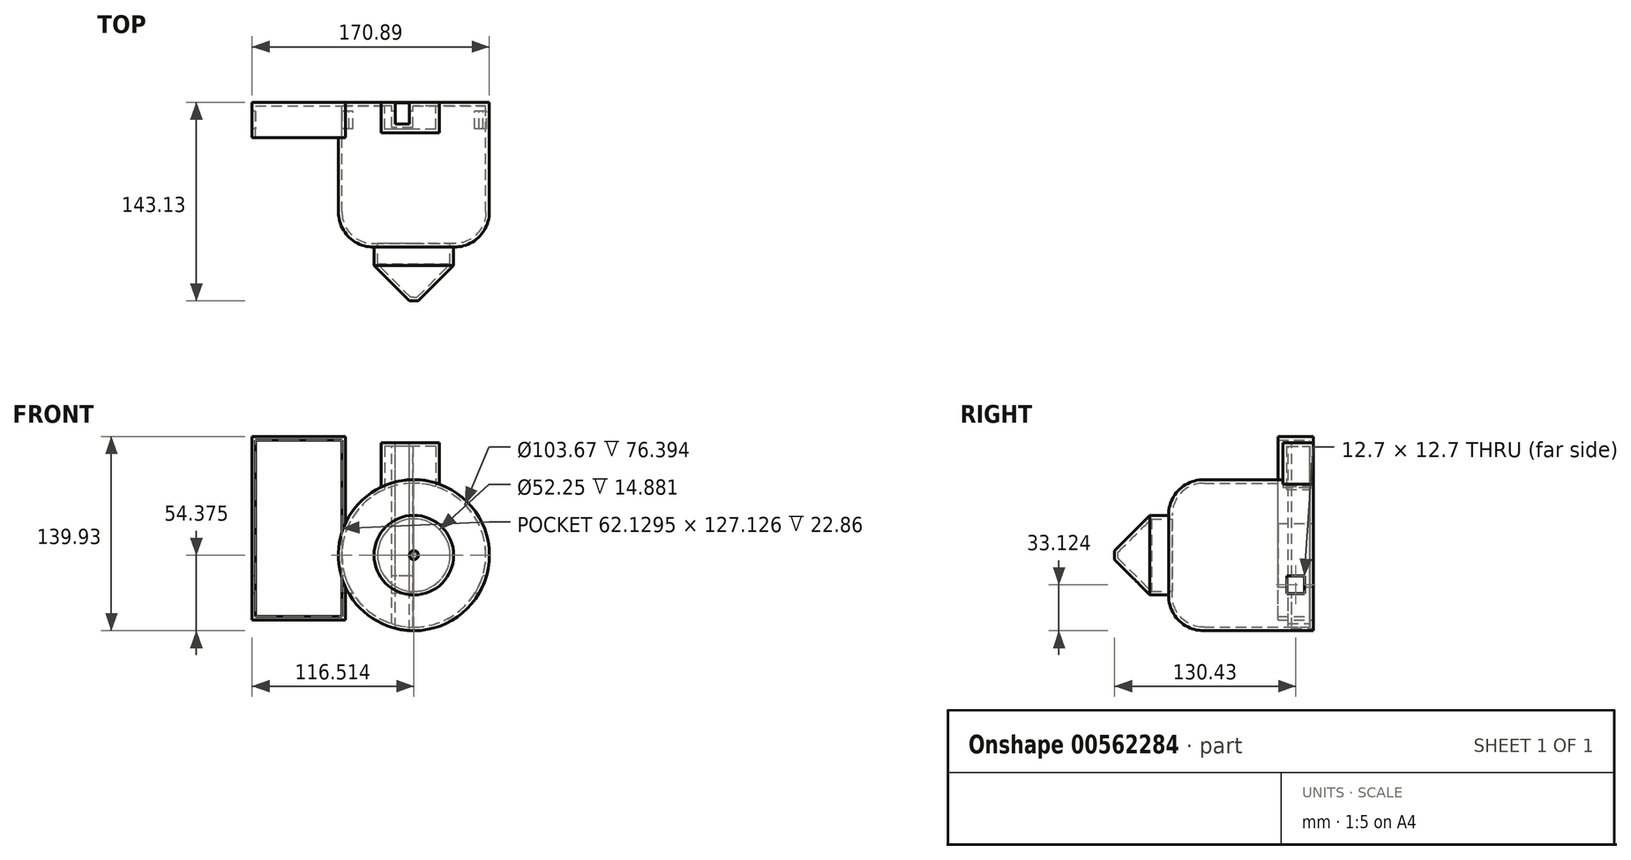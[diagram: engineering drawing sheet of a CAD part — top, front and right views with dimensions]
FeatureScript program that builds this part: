
annotation { "Feature Type Name" : "Feature", "Feature Type Description" : "" }
export const myFeature = defineFeature(function(context is Context, id is Id, definition is map)
    precondition{}
    {
        {
            var Q0;
            Q0=qCreatedBy(makeId("Front.planeOp"),FACE);
            var sketch = newSketch(context, id + "F0", { "sketchPlane" : qUnion([Q0])});
            skCircle(sketch, "E0", {"center": v(49.3, -22.93) * mm, "radius": 54.37 * mm});
            skSolve(sketch);
        }
        {
            var Q0;
            Q0 = qSketchRegion(id + "F0", true);
            extrude(context, id + "F1", {"entities" : qUnion([Q0]), "depth" : 104.33 * mm, "offsetDistance" : 25.4 * mm});
        }
        {
            var Q0;
            Q0=qCreatedBy(makeId("Front.planeOp"),FACE);
            var sketch = newSketch(context, id + "F2", { "sketchPlane" : qUnion([Q0])});
            skLineSegment(sketch, "E1.bottom", {"start": v(67.62, 57.92) * mm, "end": v(25.77, 57.92) * mm});
            skLineSegment(sketch, "E1.top", {"start": v(67.62, 15.74) * mm, "end": v(25.77, 15.74) * mm});
            skLineSegment(sketch, "E1.left", {"start": v(67.62, 57.92) * mm, "end": v(67.62, 15.74) * mm});
            skLineSegment(sketch, "E1.right", {"start": v(25.77, 57.92) * mm, "end": v(25.77, 15.74) * mm});
            skLineSegment(sketch, "E2.bottom", {"start": v(-64.32, 213.68) * mm, "end": v(12.28, 213.68) * mm});
            skLineSegment(sketch, "E2.top", {"start": v(-64.32, 129.94) * mm, "end": v(12.28, 129.94) * mm});
            skLineSegment(sketch, "E2.left", {"start": v(-64.32, 213.68) * mm, "end": v(-64.32, 129.94) * mm});
            skLineSegment(sketch, "E2.right", {"start": v(12.28, 213.68) * mm, "end": v(12.28, 129.94) * mm});
            skSolve(sketch);
        }
        {
            var Q0;
            Q0=makeQuery(id+"F2.imprint","IMPRINT",FACE,{"disambiguationData":[TD([[makeQuery(id+"F2.imprint","IMPRINT",EDGE,{"derivedFrom":sQuery(id+"F2.wireOp",EDGE,"E1.bottom")}),1.0]])]});
            extrude(context, id + "F3", {"entities" : qUnion([Q0]), "operationType" : NewBodyOperationType.ADD, "depth" : 22.02 * mm, "offsetDistance" : 25.4 * mm});
        }
        {
            var Q0;
            Q0=makeQuery(id+"F1.opExtrude","CAP_EDGE",EDGE,{"disambiguationData":[OSD([sQuery(id+"F0.wireOp",EDGE,"E0")])],"isStart":false});
            fillet(context, id + "F4", {"entities" : qUnion([Q0]), "radius" : 25.4 * mm, "tangentPropagation" : true, "allowEdgeOverflow" : false});
        }
        {
            var Q0;
            Q0=makeQuery(id+"F1.opExtrude","CAP_FACE",FACE,{"disambiguationData":[OSD([sQuery(id+"F0.wireOp",EDGE,"E0")])],"isStart":false});
            var sketch = newSketch(context, id + "F5", { "sketchPlane" : qUnion([Q0])});
            skCircle(sketch, "E3", {"center": v(49.3, -22.93) * mm, "radius": 28.66 * mm});
            skSolve(sketch);
        }
        {
            var Q0;
            Q0 = qSketchRegion(id + "F5", true);
            extrude(context, id + "F6", {"entities" : qUnion([Q0]), "operationType" : NewBodyOperationType.ADD, "depth" : 38.8 * mm, "offsetDistance" : 25.4 * mm});
        }
        {
            var Q0;
            Q0=makeQuery(id+"F6.opExtrude","CAP_EDGE",EDGE,{"disambiguationData":[OSD([sQuery(id+"F5.wireOp",EDGE,"E3")])],"isStart":false});
            chamfer(context, id + "F7", {"entities" : qUnion([Q0]), "width" : 25.4 * mm, "tangentPropagation" : true});
        }
        {
            var Q0;
            Q0=makeQuery(id+"F3.opExtrude","SWEPT_FACE",FACE,{"disambiguationData":[OSD([sQuery(id+"F2.wireOp",EDGE,"E1.bottom")])]});
            var sketch = newSketch(context, id + "F8", { "sketchPlane" : qUnion([Q0])});
            skLineSegment(sketch, "E4.bottom", {"start": v(46.1, -15.67) * mm, "end": v(35.93, -15.67) * mm});
            skLineSegment(sketch, "E4.top", {"start": v(46.1, -0.43) * mm, "end": v(35.93, -0.43) * mm});
            skLineSegment(sketch, "E4.left", {"start": v(46.1, -15.67) * mm, "end": v(46.1, -0.43) * mm});
            skLineSegment(sketch, "E4.right", {"start": v(35.93, -15.67) * mm, "end": v(35.93, -0.43) * mm});
            skSolve(sketch);
        }
        {
            var Q0;
            Q0=makeQuery(id+"F8.imprint","IMPRINT",FACE,{"disambiguationData":[TD([[makeQuery(id+"F8.imprint","IMPRINT",EDGE,{"derivedFrom":sQuery(id+"F8.wireOp",EDGE,"E4.bottom")}),-1.0]])]});
            extrude(context, id + "F9", {"entities" : qUnion([Q0]), "operationType" : NewBodyOperationType.REMOVE, "endBound" : BoundingType.THROUGH_ALL, "oppositeDirection" : true, "depth" : 25.4 * mm, "offsetDistance" : 25.4 * mm});
        }
        {
            var Q0;
            Q0=qCreatedBy(makeId("Front.planeOp"),FACE);
            var sketch = newSketch(context, id + "F10", { "sketchPlane" : qUnion([Q0])});
            skLineSegment(sketch, "E5.bottom", {"start": v(-67.2, -69.58) * mm, "end": v(0, -69.58) * mm});
            skLineSegment(sketch, "E5.top", {"start": v(-67.2, 62.63) * mm, "end": v(0, 62.63) * mm});
            skLineSegment(sketch, "E5.left", {"start": v(-67.2, -69.58) * mm, "end": v(-67.2, 62.63) * mm});
            skLineSegment(sketch, "E5.right", {"start": v(0, -69.58) * mm, "end": v(0, 62.63) * mm});
            skSolve(sketch);
        }
        {
            var Q0;
            Q0 = qSketchRegion(id + "F10", true);
            extrude(context, id + "F11", {"entities" : qUnion([Q0]), "operationType" : NewBodyOperationType.ADD, "depth" : 25.4 * mm, "offsetDistance" : 25.4 * mm});
        }
        {
            var Q0;
            Q0=makeQuery(id+"F11.opExtrude","CAP_FACE",FACE,{"disambiguationData":[OSD([sQuery(id+"F10.wireOp",EDGE,"E5.bottom"),sQuery(id+"F10.wireOp",EDGE,"E5.top"),sQuery(id+"F10.wireOp",EDGE,"E5.left"),sQuery(id+"F10.wireOp",EDGE,"E5.right")])],"isStart":false});
            shell(context, id + "F12", {"entities" : qUnion([Q0]), "thickness" : 2.54 * mm});
        }
        {
            var Q0;
            Q0=makeQuery(id+"F11.opExtrude","SWEPT_FACE",FACE,{"disambiguationData":[OSD([sQuery(id+"F10.wireOp",EDGE,"E5.left")])]});
            var sketch = newSketch(context, id + "F13", { "sketchPlane" : qUnion([Q0])});
            skLineSegment(sketch, "E6.bottom", {"start": v(6.35, -37.83) * mm, "end": v(19.05, -37.83) * mm});
            skLineSegment(sketch, "E6.top", {"start": v(6.35, -50.53) * mm, "end": v(19.05, -50.53) * mm});
            skLineSegment(sketch, "E6.left", {"start": v(6.35, -37.83) * mm, "end": v(6.35, -50.53) * mm});
            skLineSegment(sketch, "E6.right", {"start": v(19.05, -37.83) * mm, "end": v(19.05, -50.53) * mm});
            skSolve(sketch);
        }
        {
            var Q0;
            Q0=makeQuery(id+"F13.imprint","IMPRINT",FACE,{"disambiguationData":[TD([[makeQuery(id+"F13.imprint","IMPRINT",EDGE,{"derivedFrom":sQuery(id+"F13.wireOp",EDGE,"E6.bottom")}),-1.0]])]});
            extrude(context, id + "F14", {"entities" : qUnion([Q0]), "operationType" : NewBodyOperationType.REMOVE, "endBound" : BoundingType.THROUGH_ALL, "oppositeDirection" : true, "depth" : 25.4 * mm, "offsetDistance" : 25.4 * mm});
        }
    });
